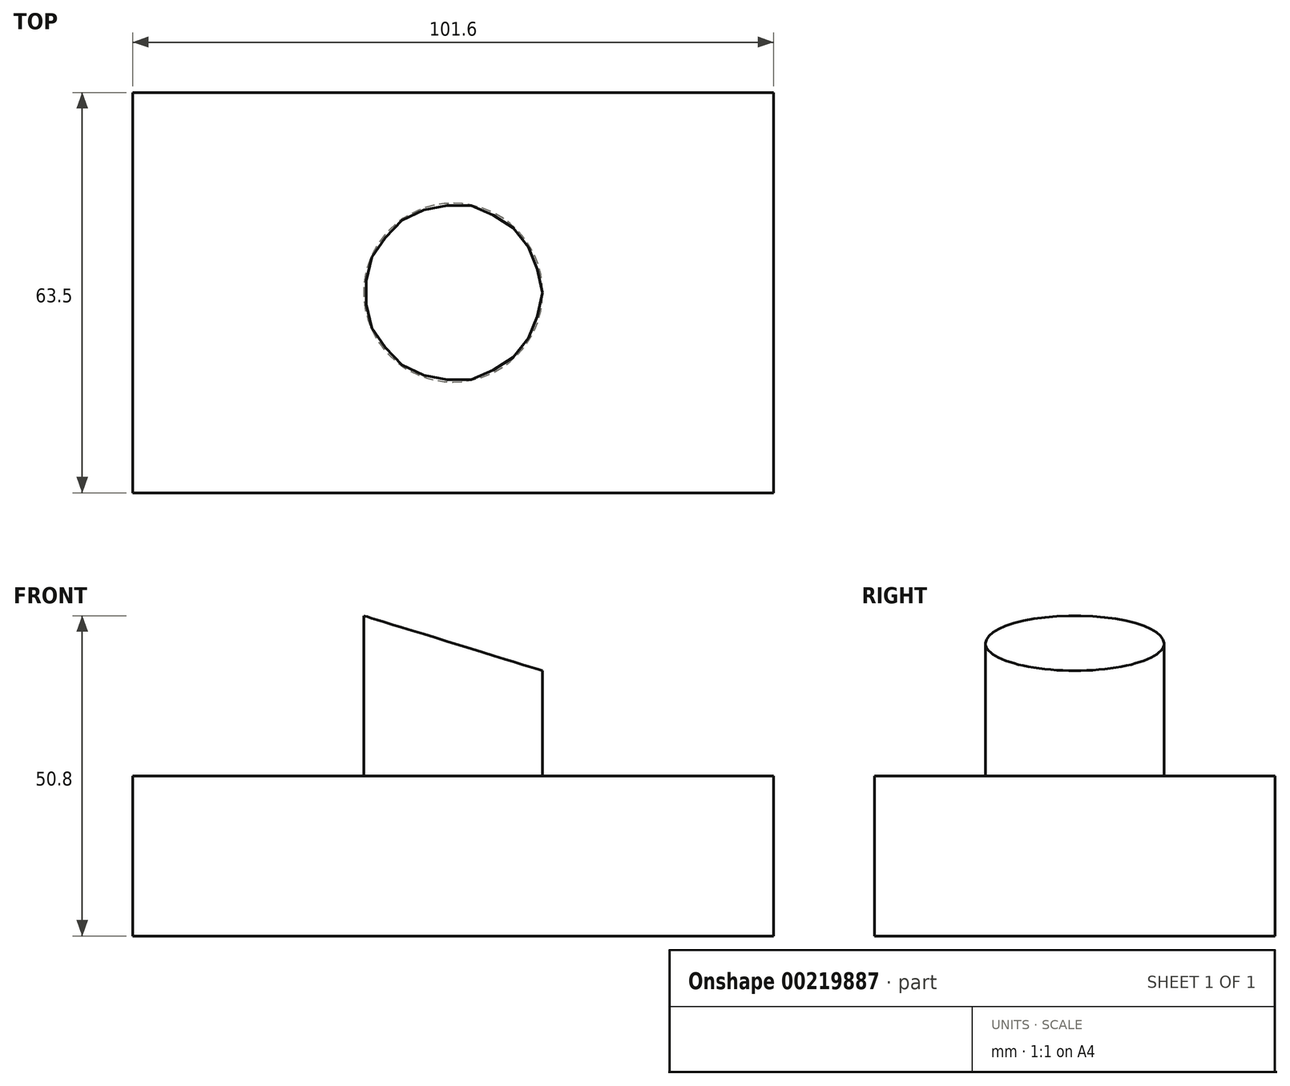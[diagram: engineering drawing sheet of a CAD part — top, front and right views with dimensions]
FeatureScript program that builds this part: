
annotation { "Feature Type Name" : "Feature", "Feature Type Description" : "" }
export const myFeature = defineFeature(function(context is Context, id is Id, definition is map)
    precondition{}
    {
        {
            var Q0;
            Q0=qCreatedBy(makeId("Top.planeOp"),FACE);
            var sketch = newSketch(context, id + "F0", { "sketchPlane" : qUnion([Q0])});
            skLineSegment(sketch, "E0.bottom", {"start": v(50.8, -31.75) * mm, "end": v(-50.8, -31.75) * mm});
            skLineSegment(sketch, "E0.top", {"start": v(50.8, 31.75) * mm, "end": v(-50.8, 31.75) * mm});
            skLineSegment(sketch, "E0.left", {"start": v(50.8, -31.75) * mm, "end": v(50.8, 31.75) * mm});
            skLineSegment(sketch, "E0.right", {"start": v(-50.8, -31.75) * mm, "end": v(-50.8, 31.75) * mm});
            skPoint(sketch, "E0.middle", {"position": v(0, 0) * mm});
            skSolve(sketch);
        }
        {
            var Q0;
            Q0=makeQuery(id+"F0.imprint","IMPRINT",FACE,{"disambiguationData":[TD([[makeQuery(id+"F0.imprint","IMPRINT",EDGE,{"derivedFrom":sQuery(id+"F0.wireOp",EDGE,"E0.bottom")}),-1.0]])]});
            var sketch = newSketch(context, id + "F1", { "sketchPlane" : qUnion([Q0])});
            skCircle(sketch, "E1", {"center": v(0, 0) * mm, "radius": 14.19 * mm});
            skSolve(sketch);
        }
        {
            var Q0;
            Q0=makeQuery(id+"F0.imprint","IMPRINT",FACE,{"disambiguationData":[TD([[makeQuery(id+"F0.imprint","IMPRINT",EDGE,{"derivedFrom":sQuery(id+"F0.wireOp",EDGE,"E0.bottom")}),-1.0]])]});
            extrude(context, id + "F2", {"entities" : qUnion([Q0]), "depth" : 25.4 * mm});
        }
        {
            var Q0;
            Q0 = qSketchRegion(id + "F1", true);
            extrude(context, id + "F3", {"entities" : qUnion([Q0]), "operationType" : NewBodyOperationType.ADD, "depth" : 50.8 * mm});
        }
        {
            var Q0;
            Q0=qCreatedBy(makeId("Front.planeOp"),FACE);
            var sketch = newSketch(context, id + "F4", { "sketchPlane" : qUnion([Q0])});
            skLineSegment(sketch, "E2.0", {"start": v(-14.19, 50.8) * mm, "end": v(14.19, 50.8) * mm});
            skLineSegment(sketch, "E3", {"start": v(14.19, 50.8) * mm, "end": v(14.19, 42.07) * mm});
            skLineSegment(sketch, "E4", {"start": v(14.19, 42.07) * mm, "end": v(-14.19, 50.8) * mm});
            skSolve(sketch);
        }
        {
            var Q0;
            Q0 = qSketchRegion(id + "F4", true);
            extrude(context, id + "F5", {"entities" : qUnion([Q0]), "operationType" : NewBodyOperationType.REMOVE, "endBound" : BoundingType.SYMMETRIC, "oppositeDirection" : true, "depth" : 50.8 * mm});
        }
    });
